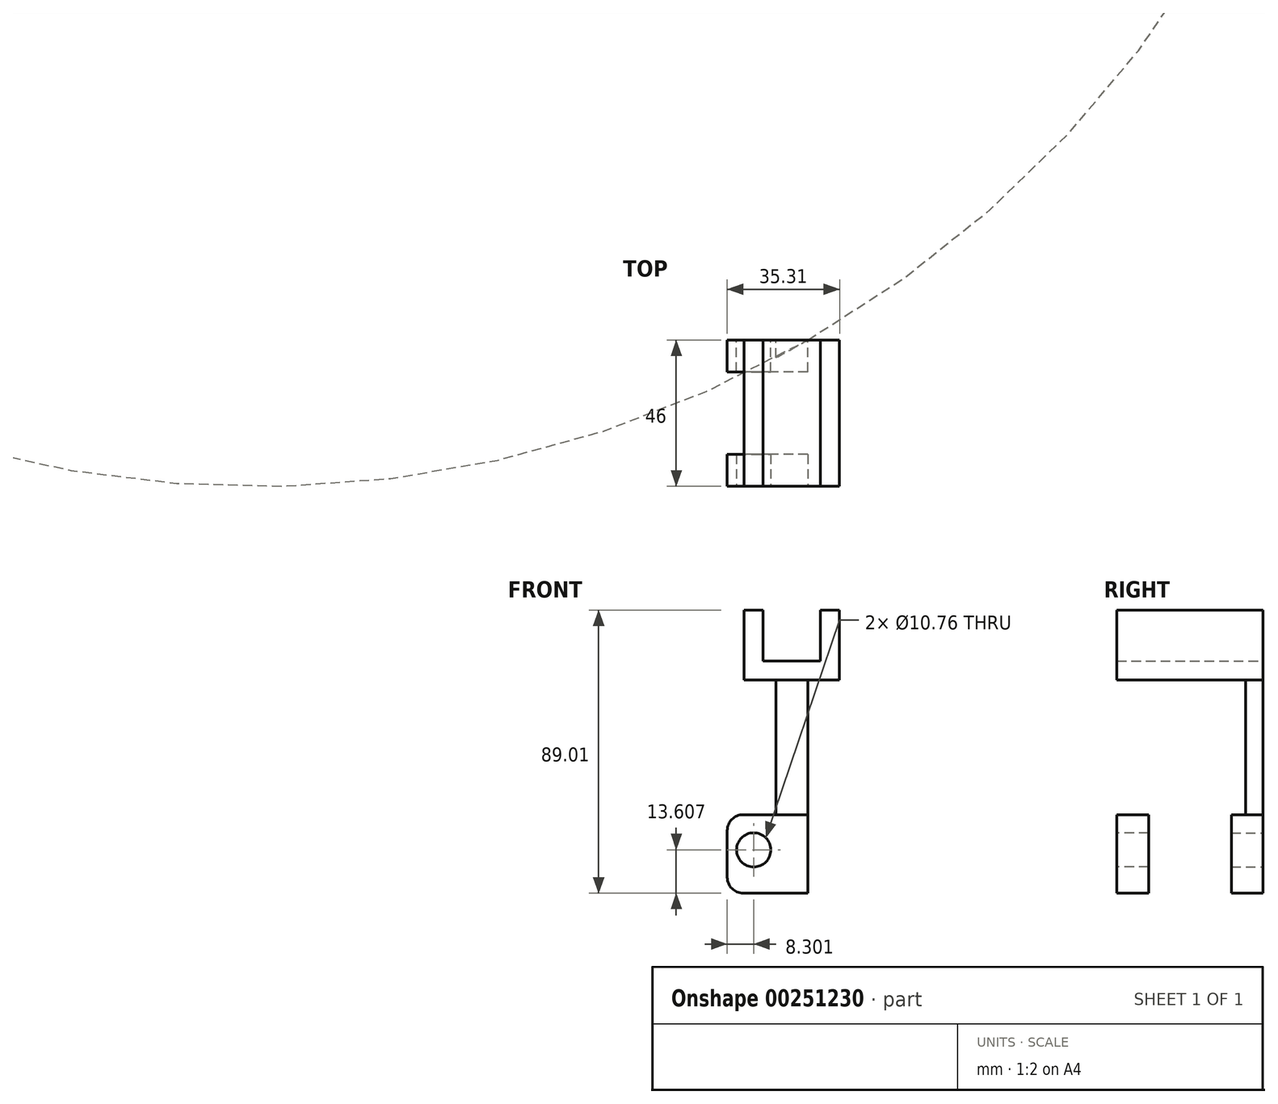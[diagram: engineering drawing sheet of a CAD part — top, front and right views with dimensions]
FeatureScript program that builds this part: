
annotation { "Feature Type Name" : "Feature", "Feature Type Description" : "" }
export const myFeature = defineFeature(function(context is Context, id is Id, definition is map)
    precondition{}
    {
        {
            var Q0;
            Q0=qCreatedBy(makeId("Front.planeOp"),FACE);
            var sketch = newSketch(context, id + "F0", { "sketchPlane" : qUnion([Q0])});
            skLineSegment(sketch, "E0", {"start": v(-59.72, 34.05) * mm, "end": v(-53.72, 34.05) * mm});
            skLineSegment(sketch, "E1", {"start": v(-59.72, 34.05) * mm, "end": v(-59.72, 12.05) * mm});
            skLineSegment(sketch, "E2", {"start": v(-59.72, 12.05) * mm, "end": v(-49.72, 12.05) * mm});
            skLineSegment(sketch, "E3", {"start": v(-49.72, 12.05) * mm, "end": v(-49.72, -54.95) * mm});
            skLineSegment(sketch, "E4", {"start": v(-53.72, 34.05) * mm, "end": v(-53.72, 18.05) * mm});
            skLineSegment(sketch, "E5", {"start": v(-53.72, 18.05) * mm, "end": v(-35.72, 18.05) * mm});
            skLineSegment(sketch, "E6", {"start": v(-35.72, 18.05) * mm, "end": v(-35.72, 34.05) * mm});
            skLineSegment(sketch, "E7", {"start": v(-35.72, 34.05) * mm, "end": v(-29.72, 34.05) * mm});
            skLineSegment(sketch, "E8", {"start": v(-29.72, 34.05) * mm, "end": v(-29.72, 12.05) * mm});
            skLineSegment(sketch, "E9", {"start": v(-29.72, 12.05) * mm, "end": v(-39.72, 12.05) * mm});
            skLineSegment(sketch, "E10", {"start": v(-39.72, 12.05) * mm, "end": v(-39.72, -54.95) * mm});
            skLineSegment(sketch, "E11", {"start": v(-49.72, -54.95) * mm, "end": v(-39.72, -54.95) * mm});
            skSolve(sketch);
        }
        {
            var Q0;
            Q0 = qSketchRegion(id + "F0", true);
            extrude(context, id + "F1", {"entities" : qUnion([Q0]), "depth" : 46 * mm});
        }
        {
            var Q0;
            Q0=makeQuery(id+"FMuEhtr0SY8AsnH_0.opExtrude","SWEPT_EDGE",EDGE,{"disambiguationData":[OSD([sQuery(id+"FWowiUMUTH0BHuY_1.wireOp",EDGE,"yhZOauMZ-Ss3c-tK4F-8XdK-BKKr0fSDhdYE"),sQuery(id+"FWowiUMUTH0BHuY_1.wireOp",EDGE,"cXXkoK4v-cZjY-9dqU-Xs9Y-qJzcYOkk61mT")])]});
            var Q1;
            Q1=makeQuery(id+"FMuEhtr0SY8AsnH_0.opExtrude","CAP_EDGE",EDGE,{"disambiguationData":[OSD([sQuery(id+"FWowiUMUTH0BHuY_1.wireOp",EDGE,"cXXkoK4v-cZjY-9dqU-Xs9Y-qJzcYOkk61mT"),sQuery(id+"FWowiUMUTH0BHuY_1.wireOp",EDGE,"LSwmAZEy-Vctw-uPnm-3TIY-lC3FUWTE54za")])],"isStart":false});
            var Q2;
            Q2=makeQuery(id+"FMuEhtr0SY8AsnH_0.opExtrude","CAP_EDGE",EDGE,{"disambiguationData":[OSD([sQuery(id+"FWowiUMUTH0BHuY_1.wireOp",EDGE,"yocHBjtr-VkP3-9nvR-iIW7-ismoY3b0hpkn"),sQuery(id+"FWowiUMUTH0BHuY_1.wireOp",EDGE,"InL04ASf-VbdZ-b2Rh-Vgpi-6SFFBhuqv7tL")])],"isStart":false});
            var Q3;
            Q3=makeQuery(id+"FMuEhtr0SY8AsnH_0.opExtrude","SWEPT_FACE",FACE,{"disambiguationData":[OSD([sQuery(id+"FWowiUMUTH0BHuY_1.wireOp",EDGE,"cXXkoK4v-cZjY-9dqU-Xs9Y-qJzcYOkk61mT"),sQuery(id+"FWowiUMUTH0BHuY_1.wireOp",EDGE,"LSwmAZEy-Vctw-uPnm-3TIY-lC3FUWTE54za")])]});
            var Q4;
            Q4=makeQuery(id+"F1.opExtrude","CAP_EDGE",EDGE,{"disambiguationData":[OSD([sQuery(id+"F0.wireOp",EDGE,"E10")])],"isStart":false});
            var Q5;
            Q5=makeQuery(id+"FMuEhtr0SY8AsnH_0.opExtrude","CAP_FACE",FACE,{"disambiguationData":[OSD([sQuery(id+"FWowiUMUTH0BHuY_1.wireOp",EDGE,"oZYPnYuj-lC46-Oyq3-qU36-Vva6Hw66EEaH"),sQuery(id+"FWowiUMUTH0BHuY_1.wireOp",EDGE,"yhZOauMZ-Ss3c-tK4F-8XdK-BKKr0fSDhdYE"),sQuery(id+"FWowiUMUTH0BHuY_1.wireOp",EDGE,"cXXkoK4v-cZjY-9dqU-Xs9Y-qJzcYOkk61mT"),sQuery(id+"FWowiUMUTH0BHuY_1.wireOp",EDGE,"LSwmAZEy-Vctw-uPnm-3TIY-lC3FUWTE54za"),sQuery(id+"FWowiUMUTH0BHuY_1.wireOp",EDGE,"yocHBjtr-VkP3-9nvR-iIW7-ismoY3b0hpkn"),sQuery(id+"FWowiUMUTH0BHuY_1.wireOp",EDGE,"InL04ASf-VbdZ-b2Rh-Vgpi-6SFFBhuqv7tL"),sQuery(id+"FWowiUMUTH0BHuY_1.wireOp",EDGE,"TgDw4g4M-62oF-dSMN-AdGN-NPDBEzgiUoMV"),sQuery(id+"FWowiUMUTH0BHuY_1.wireOp",EDGE,"HNAnYzm8-deVu-VKRN-KI4M-Uk8Wn2weKp5Z"),sQuery(id+"FWowiUMUTH0BHuY_1.wireOp",EDGE,"moybwfIq-aKh3-5ndg-c5Lc-ak88Aas55dmE")])],"isStart":false});
            var Q6;
            Q6=makeQuery(id+"FMuEhtr0SY8AsnH_0.opExtrude","SWEPT_EDGE",EDGE,{"disambiguationData":[OSD([sQuery(id+"FWowiUMUTH0BHuY_1.wireOp",EDGE,"LSwmAZEy-Vctw-uPnm-3TIY-lC3FUWTE54za"),sQuery(id+"FWowiUMUTH0BHuY_1.wireOp",EDGE,"yocHBjtr-VkP3-9nvR-iIW7-ismoY3b0hpkn")])]});
            fillet(context, id + "F2", {"entities" : qUnion([Q0, Q1, Q2, Q3, Q4, Q5, Q6]), "radius" : 348.13 * mm, "tangentPropagation" : true, "allowEdgeOverflow" : false});
        }
        {
            var Q0;
            Q0=makeQuery(id+"F1.opExtrude","CAP_FACE",FACE,{"disambiguationData":[OSD([sQuery(id+"F0.wireOp",EDGE,"E0"),sQuery(id+"F0.wireOp",EDGE,"E1"),sQuery(id+"F0.wireOp",EDGE,"E2"),sQuery(id+"F0.wireOp",EDGE,"E3"),sQuery(id+"F0.wireOp",EDGE,"E4"),sQuery(id+"F0.wireOp",EDGE,"E5"),sQuery(id+"F0.wireOp",EDGE,"E6"),sQuery(id+"F0.wireOp",EDGE,"E7"),sQuery(id+"F0.wireOp",EDGE,"E8"),sQuery(id+"F0.wireOp",EDGE,"E9"),sQuery(id+"F0.wireOp",EDGE,"E10"),sQuery(id+"F0.wireOp",EDGE,"E11")])],"isStart":true});
            var sketch = newSketch(context, id + "F3", { "sketchPlane" : qUnion([Q0])});
            skLineSegment(sketch, "E12.bottom", {"start": v(39.72, -30.28) * mm, "end": v(60.03, -30.28) * mm});
            skLineSegment(sketch, "E12.top", {"start": v(39.72, -54.96) * mm, "end": v(60.03, -54.96) * mm});
            skLineSegment(sketch, "E12.left", {"start": v(39.72, -30.28) * mm, "end": v(39.72, -54.96) * mm});
            skLineSegment(sketch, "E12.right", {"start": v(65.03, -35.28) * mm, "end": v(65.03, -49.96) * mm});
            skCircle(sketch, "E13", {"center": v(56.73, -41.35) * mm, "radius": 5.38 * mm});
            skPoint(sketch, "E14.visualSharp", {"position": v(65.03, -30.28) * mm});
            skArc(sketch, "E14.filletArc", {"start": v(65.03, -35.28) * mm, "mid": v(63.57, -31.75) * mm, "end": v(60.03, -30.28) * mm});
            skPoint(sketch, "E15.visualSharp", {"position": v(65.03, -54.96) * mm});
            skArc(sketch, "E15.filletArc", {"start": v(60.03, -54.96) * mm, "mid": v(63.57, -53.5) * mm, "end": v(65.03, -49.96) * mm});
            skPoint(sketch, "E16.orphan", {"position": v(39.72, -55.37) * mm});
            skSolve(sketch);
        }
        {
            var Q0;
            Q0 = qSketchRegion(id + "F3", true);
            extrude(context, id + "F4", {"entities" : qUnion([Q0]), "oppositeDirection" : true, "depth" : 10 * mm});
        }
        {
            var Q0;
            Q0=makeQuery(id+"F1.opExtrude","SWEPT_EDGE",EDGE,{"disambiguationData":[OSD([sQuery(id+"F0.wireOp",EDGE,"E0"),sQuery(id+"F0.wireOp",EDGE,"E1")])]});
            cPoint(context, id + "F5", {"entities" : qUnion([Q0]), "parameter" : 0.5});
        }
        {
            var Q0;
            Q0=makeQuery(id+"F1.opExtrude","SWEPT_EDGE",EDGE,{"disambiguationData":[OSD([sQuery(id+"F0.wireOp",EDGE,"E1"),sQuery(id+"F0.wireOp",EDGE,"E2")])]});
            cPoint(context, id + "F6", {"entities" : qUnion([Q0]), "parameter" : 0.5});
        }
        {
            var Q0;
            Q0=makeQuery(id+"F1.opExtrude","SWEPT_EDGE",EDGE,{"disambiguationData":[OSD([sQuery(id+"F0.wireOp",EDGE,"E7"),sQuery(id+"F0.wireOp",EDGE,"E8")])]});
            cPoint(context, id + "F7", {"entities" : qUnion([Q0]), "parameter" : 0.5});
        }
        {
            var Q0;
            Q0 = qCreatedBy(id + "F5" ,VERTEX);
            var Q1;
            Q1 = qCreatedBy(id + "F6" ,VERTEX);
            var Q2;
            Q2 = qCreatedBy(id + "F7" ,VERTEX);
            cPlane(context, id + "F8", {"entities" : qUnion([Q0, Q1, Q2]), "cplaneType" : CPlaneType.THREE_POINT, "offset" : 25 * mm, "width" : 150 * mm, "height" : 150 * mm});
        }
        {
            var Q0;
            Q0=makeQuery(id+"F4.opExtrude","SWEPT_BODY",BODY,{"disambiguationData":[OSD([sQuery(id+"F3.wireOp",EDGE,"E12.bottom"),sQuery(id+"F3.wireOp",EDGE,"E12.top"),sQuery(id+"F3.wireOp",EDGE,"E12.left"),sQuery(id+"F3.wireOp",EDGE,"E12.right"),sQuery(id+"F3.wireOp",EDGE,"E13"),sQuery(id+"F3.wireOp",EDGE,"E14.filletArc"),sQuery(id+"F3.wireOp",EDGE,"E15.filletArc")])]});
            var Q1;
            Q1=qCreatedBy(id+"F8.planeOp",FACE);
            mirror(context, id + "F9", {"operationType" : NewBodyOperationType.ADD, "entities" : qUnion([Q0]), "mirrorPlane" : qUnion([Q1])});
        }
    });
